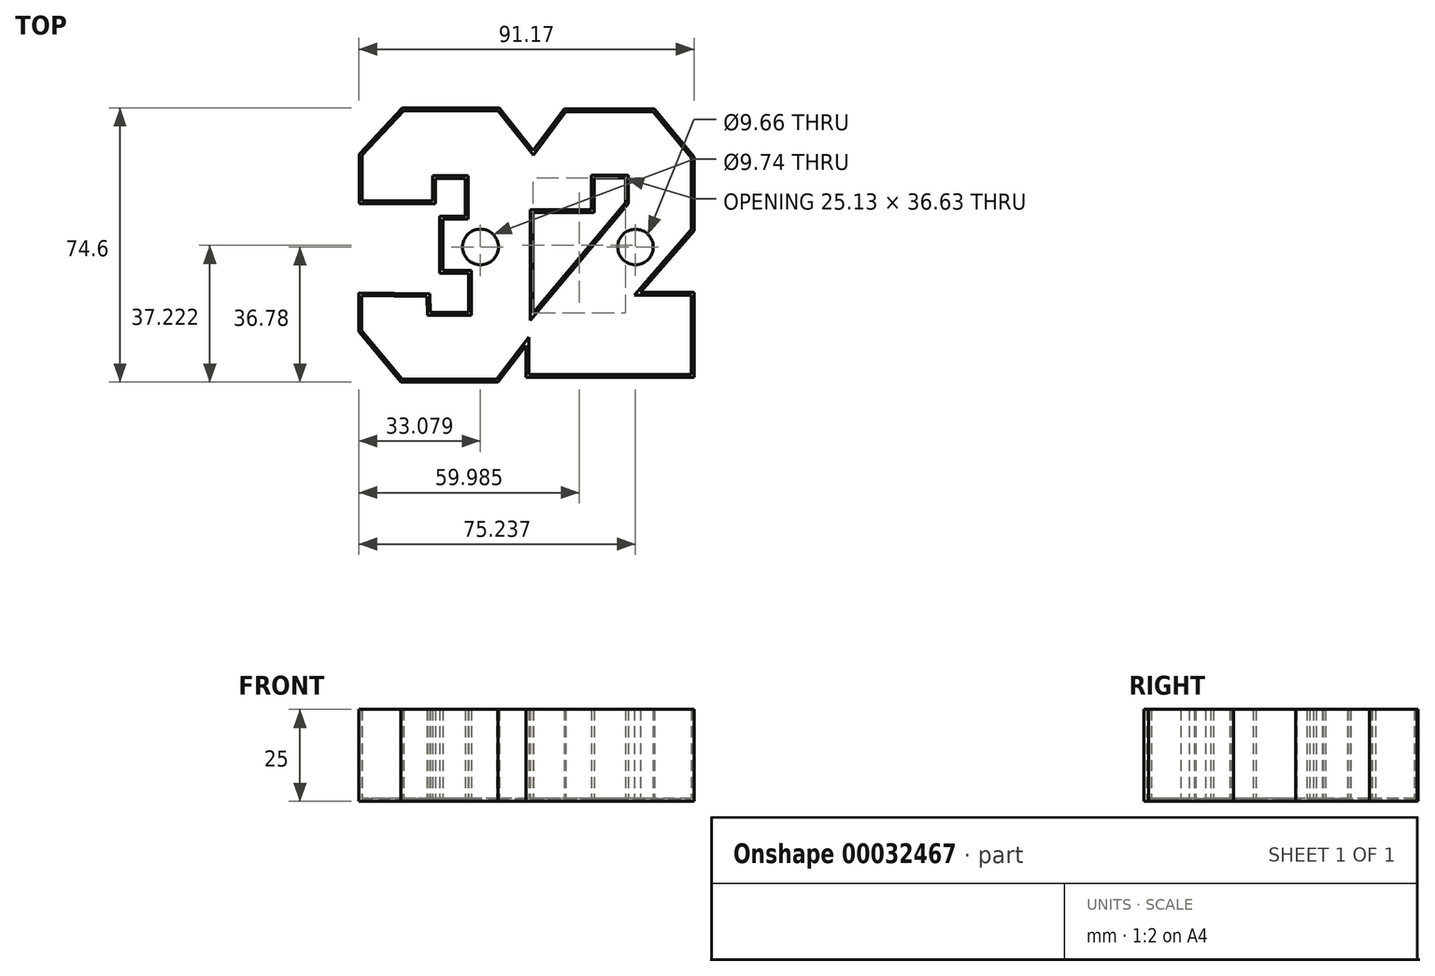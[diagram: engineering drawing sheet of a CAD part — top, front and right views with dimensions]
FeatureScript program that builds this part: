
annotation { "Feature Type Name" : "Feature", "Feature Type Description" : "" }
export const myFeature = defineFeature(function(context is Context, id is Id, definition is map)
    precondition{}
    {
        {
            var Q0;
            Q0=qCreatedBy(makeId("Top.planeOp"),FACE);
            var sketch = newSketch(context, id + "F0", { "sketchPlane" : qUnion([Q0])});
            skCircle(sketch, "E0", {"center": v(0, 0) * mm, "radius": 65.2 * mm});
            skSolve(sketch);
        }
        {
            var Q0;
            Q0=makeQuery(id+"F0.imprint","IMPRINT",FACE,{"disambiguationData":[TD([[makeQuery(id+"F0.imprint","IMPRINT",EDGE,{"derivedFrom":sQuery(id+"F0.wireOp",EDGE,"E0")}),1.0]])]});
            var sketch = newSketch(context, id + "F1", { "sketchPlane" : qUnion([Q0])});
            skLineSegment(sketch, "E1", {"start": v(0, 26.25) * mm, "end": v(8.41, 37.57) * mm});
            skLineSegment(sketch, "E2", {"start": v(8.41, 37.57) * mm, "end": v(32.95, 37.57) * mm});
            skLineSegment(sketch, "E3", {"start": v(32.95, 37.57) * mm, "end": v(43.75, 24.54) * mm});
            skLineSegment(sketch, "E4", {"start": v(43.75, 24.54) * mm, "end": v(43.75, 4.47) * mm});
            skLineSegment(sketch, "E5", {"start": v(43.75, 4.47) * mm, "end": v(29.17, -12.35) * mm});
            skLineSegment(sketch, "E6", {"start": v(29.17, -12.35) * mm, "end": v(43.75, -12.35) * mm});
            skLineSegment(sketch, "E7", {"start": v(43.75, -12.35) * mm, "end": v(43.75, -35.51) * mm});
            skLineSegment(sketch, "E8", {"start": v(43.75, -35.51) * mm, "end": v(-1.89, -35.51) * mm});
            skLineSegment(sketch, "E9", {"start": v(-1.89, -35.51) * mm, "end": v(-1.89, -26.76) * mm});
            skLineSegment(sketch, "E10", {"start": v(-28.14, -12.7) * mm, "end": v(-27.97, -17.84) * mm});
            skCircle(sketch, "E11", {"center": v(0, 0) * mm, "radius": 65.5 * mm});
            skLineSegment(sketch, "E12", {"start": v(-1.89, -26.76) * mm, "end": v(-9.52, -36.78) * mm});
            skLineSegment(sketch, "E13", {"start": v(-9.52, -36.78) * mm, "end": v(-35.92, -36.78) * mm});
            skLineSegment(sketch, "E14", {"start": v(-35.92, -36.78) * mm, "end": v(-47.42, -23.02) * mm});
            skLineSegment(sketch, "E15", {"start": v(-47.42, -23.02) * mm, "end": v(-47.42, -12.52) * mm});
            skLineSegment(sketch, "E16", {"start": v(-47.42, -12.52) * mm, "end": v(-28.14, -12.7) * mm});
            skLineSegment(sketch, "E17", {"start": v(-27.97, -17.84) * mm, "end": v(-17.55, -17.84) * mm});
            skLineSegment(sketch, "E18", {"start": v(-17.55, -17.84) * mm, "end": v(-17.55, -7.08) * mm});
            skLineSegment(sketch, "E19", {"start": v(-17.55, -7.08) * mm, "end": v(-25.39, -7.08) * mm});
            skLineSegment(sketch, "E20", {"start": v(-25.39, -7.08) * mm, "end": v(-25.39, 8.35) * mm});
            skLineSegment(sketch, "E21", {"start": v(-25.39, 8.35) * mm, "end": v(-18.47, 8.35) * mm});
            skLineSegment(sketch, "E22", {"start": v(-18.47, 8.35) * mm, "end": v(-18.47, 18.62) * mm});
            skLineSegment(sketch, "E23", {"start": v(-18.47, 18.62) * mm, "end": v(-26.6, 18.62) * mm});
            skLineSegment(sketch, "E24", {"start": v(-26.6, 18.62) * mm, "end": v(-26.6, 11.8) * mm});
            skLineSegment(sketch, "E25", {"start": v(-26.6, 11.8) * mm, "end": v(-47.32, 11.8) * mm});
            skLineSegment(sketch, "E26", {"start": v(-47.32, 11.8) * mm, "end": v(-47.32, 25.29) * mm});
            skLineSegment(sketch, "E27", {"start": v(-47.32, 25.29) * mm, "end": v(-35.55, 37.82) * mm});
            skLineSegment(sketch, "E28", {"start": v(-35.55, 37.82) * mm, "end": v(-9.23, 37.82) * mm});
            skLineSegment(sketch, "E29", {"start": v(-9.23, 37.82) * mm, "end": v(0, 26.25) * mm});
            skLineSegment(sketch, "E30", {"start": v(-2.16, 28.95) * mm, "end": v(-2.16, 65.47) * mm});
            skLineSegment(sketch, "E31", {"start": v(-2.16, 65.47) * mm, "end": v(2.16, 65.47) * mm});
            skLineSegment(sketch, "E32", {"start": v(2.16, 65.47) * mm, "end": v(2.16, 29.15) * mm});
            skLineSegment(sketch, "E33", {"start": v(0, 26.25) * mm, "end": v(0, 9.38) * mm});
            skLineSegment(sketch, "E34", {"start": v(0, 9.38) * mm, "end": v(16.63, 9.38) * mm});
            skLineSegment(sketch, "E35", {"start": v(16.63, 9.38) * mm, "end": v(16.63, 18.76) * mm});
            skLineSegment(sketch, "E36", {"start": v(16.63, 18.76) * mm, "end": v(25.13, 18.76) * mm});
            skLineSegment(sketch, "E37", {"start": v(25.13, 18.76) * mm, "end": v(25.13, 12.03) * mm});
            skLineSegment(sketch, "E38", {"start": v(25.13, 12.03) * mm, "end": v(0, -17.87) * mm});
            skLineSegment(sketch, "E39", {"start": v(0, -17.87) * mm, "end": v(0, 9.38) * mm});
            skLineSegment(sketch, "E40", {"start": v(-1.89, -26.76) * mm, "end": v(0, -17.87) * mm});
            skSolve(sketch);
        }
        {
            var Q0;
            Q0=makeQuery(id+"F1.imprint","IMPRINT",FACE,{"disambiguationData":[TD([[makeQuery(id+"F1.imprint","IMPRINT",EDGE,{"derivedFrom":sQuery(id+"F1.wireOp",EDGE,"E10")}),-1.0]])]});
            var Q1;
            {var subQ1=sQuery(id+"F1.wireOp",EDGE,"E2");Q1=makeQuery(id+"F1.imprint","IMPRINT",FACE,{"disambiguationData":[TD([[makeQuery(id+"F1.imprint","IMPRINT",EDGE,{"derivedFrom":subQ1}),-1.0]])]});}
            extrude(context, id + "F2", {"entities" : qUnion([Q0, Q1]), "depth" : 25 * mm});
        }
        {
            var Q0;
            Q0=makeQuery(id+"F2.opExtrude","CAP_FACE",FACE,{"disambiguationData":[OSD([sQuery(id+"F1.wireOp",EDGE,"E1"),sQuery(id+"F1.wireOp",EDGE,"E2"),sQuery(id+"F1.wireOp",EDGE,"E3"),sQuery(id+"F1.wireOp",EDGE,"E4"),sQuery(id+"F1.wireOp",EDGE,"E5"),sQuery(id+"F1.wireOp",EDGE,"E6"),sQuery(id+"F1.wireOp",EDGE,"E7"),sQuery(id+"F1.wireOp",EDGE,"E8"),sQuery(id+"F1.wireOp",EDGE,"E9"),sQuery(id+"F1.wireOp",EDGE,"E10"),sQuery(id+"F1.wireOp",EDGE,"E12"),sQuery(id+"F1.wireOp",EDGE,"E13"),sQuery(id+"F1.wireOp",EDGE,"E14"),sQuery(id+"F1.wireOp",EDGE,"E15"),sQuery(id+"F1.wireOp",EDGE,"E16"),sQuery(id+"F1.wireOp",EDGE,"E17"),sQuery(id+"F1.wireOp",EDGE,"E18"),sQuery(id+"F1.wireOp",EDGE,"E19"),sQuery(id+"F1.wireOp",EDGE,"E20"),sQuery(id+"F1.wireOp",EDGE,"E21"),sQuery(id+"F1.wireOp",EDGE,"E22"),sQuery(id+"F1.wireOp",EDGE,"E23"),sQuery(id+"F1.wireOp",EDGE,"E24"),sQuery(id+"F1.wireOp",EDGE,"E25"),sQuery(id+"F1.wireOp",EDGE,"E26"),sQuery(id+"F1.wireOp",EDGE,"E27"),sQuery(id+"F1.wireOp",EDGE,"E28"),sQuery(id+"F1.wireOp",EDGE,"E29"),sQuery(id+"F1.wireOp",EDGE,"E34"),sQuery(id+"F1.wireOp",EDGE,"E35"),sQuery(id+"F1.wireOp",EDGE,"E36"),sQuery(id+"F1.wireOp",EDGE,"E37"),sQuery(id+"F1.wireOp",EDGE,"E38"),sQuery(id+"F1.wireOp",EDGE,"E39")])],"isStart":false});
            shell(context, id + "F3", {"entities" : qUnion([Q0]), "thickness" : 0.76 * mm});
        }
        {
            var Q0;
            Q0=makeQuery(id+"F2.opExtrude","CAP_FACE",FACE,{"disambiguationData":[OSD([sQuery(id+"F1.wireOp",EDGE,"E1"),sQuery(id+"F1.wireOp",EDGE,"E2"),sQuery(id+"F1.wireOp",EDGE,"E3"),sQuery(id+"F1.wireOp",EDGE,"E4"),sQuery(id+"F1.wireOp",EDGE,"E5"),sQuery(id+"F1.wireOp",EDGE,"E6"),sQuery(id+"F1.wireOp",EDGE,"E7"),sQuery(id+"F1.wireOp",EDGE,"E8"),sQuery(id+"F1.wireOp",EDGE,"E9"),sQuery(id+"F1.wireOp",EDGE,"E10"),sQuery(id+"F1.wireOp",EDGE,"E12"),sQuery(id+"F1.wireOp",EDGE,"E13"),sQuery(id+"F1.wireOp",EDGE,"E14"),sQuery(id+"F1.wireOp",EDGE,"E15"),sQuery(id+"F1.wireOp",EDGE,"E16"),sQuery(id+"F1.wireOp",EDGE,"E17"),sQuery(id+"F1.wireOp",EDGE,"E18"),sQuery(id+"F1.wireOp",EDGE,"E19"),sQuery(id+"F1.wireOp",EDGE,"E20"),sQuery(id+"F1.wireOp",EDGE,"E21"),sQuery(id+"F1.wireOp",EDGE,"E22"),sQuery(id+"F1.wireOp",EDGE,"E23"),sQuery(id+"F1.wireOp",EDGE,"E24"),sQuery(id+"F1.wireOp",EDGE,"E25"),sQuery(id+"F1.wireOp",EDGE,"E26"),sQuery(id+"F1.wireOp",EDGE,"E27"),sQuery(id+"F1.wireOp",EDGE,"E28"),sQuery(id+"F1.wireOp",EDGE,"E29"),sQuery(id+"F1.wireOp",EDGE,"E34"),sQuery(id+"F1.wireOp",EDGE,"E35"),sQuery(id+"F1.wireOp",EDGE,"E36"),sQuery(id+"F1.wireOp",EDGE,"E37"),sQuery(id+"F1.wireOp",EDGE,"E38"),sQuery(id+"F1.wireOp",EDGE,"E39")])],"isStart":true});
            var sketch = newSketch(context, id + "F4", { "sketchPlane" : qUnion([Q0])});
            skCircle(sketch, "E41", {"center": v(-14.34, 0) * mm, "radius": 4.87 * mm});
            skCircle(sketch, "E42", {"center": v(27.82, 0) * mm, "radius": 4.83 * mm});
            skSolve(sketch);
        }
        {
            var Q0;
            Q0 = qSketchRegion(id + "F4", true);
            extrude(context, id + "F5", {"entities" : qUnion([Q0]), "operationType" : NewBodyOperationType.REMOVE, "oppositeDirection" : true, "depth" : 25 * mm});
        }
    });
